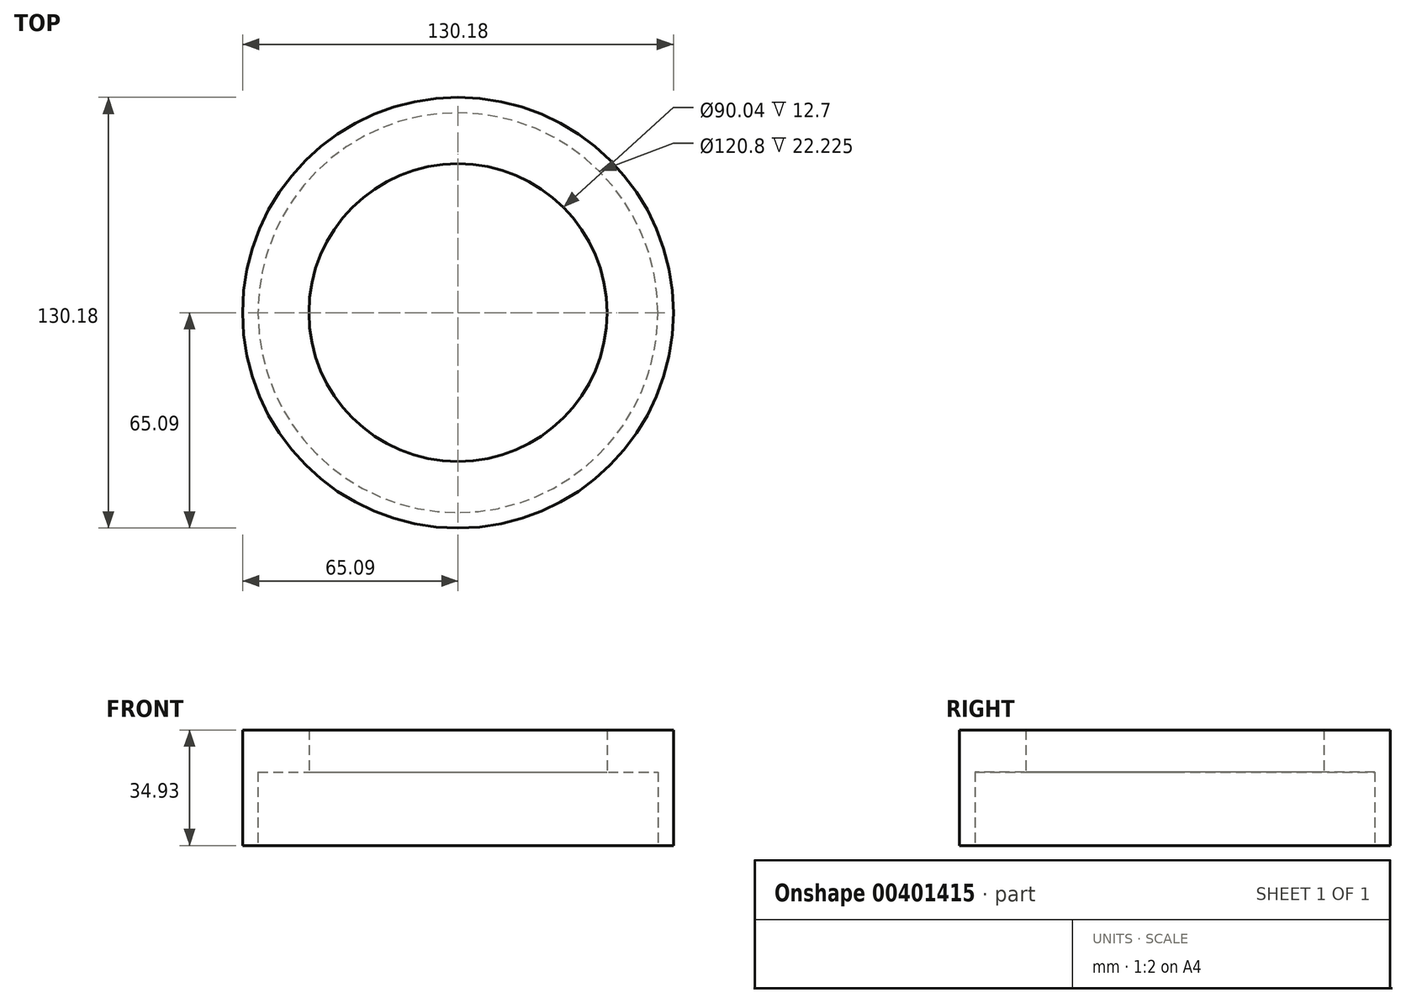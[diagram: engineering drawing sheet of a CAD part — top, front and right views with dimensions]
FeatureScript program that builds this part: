
annotation { "Feature Type Name" : "Feature", "Feature Type Description" : "" }
export const myFeature = defineFeature(function(context is Context, id is Id, definition is map)
    precondition{}
    {
        {
            var Q0;
            Q0=qCreatedBy(makeId("Top.planeOp"),FACE);
            var sketch = newSketch(context, id + "F0", { "sketchPlane" : qUnion([Q0])});
            skCircle(sketch, "E0", {"center": v(0, 0) * mm, "radius": 65.09 * mm});
            skSolve(sketch);
        }
        {
            var Q0;
            Q0=makeQuery(id+"F0.imprint","IMPRINT",FACE,{"disambiguationData":[TD([[makeQuery(id+"F0.imprint","IMPRINT",EDGE,{"derivedFrom":sQuery(id+"F0.wireOp",EDGE,"E0")}),1.0]])]});
            extrude(context, id + "F1", {"entities" : qUnion([Q0]), "oppositeDirection" : true, "depth" : 34.92 * mm});
        }
        {
            var Q0;
            Q0=makeQuery(id+"F1.opExtrude","CAP_FACE",FACE,{"disambiguationData":[OSD([sQuery(id+"F0.wireOp",EDGE,"E0")])],"isStart":false});
            var sketch = newSketch(context, id + "F2", { "sketchPlane" : qUnion([Q0])});
            skCircle(sketch, "E1", {"center": v(0, 0) * mm, "radius": 60.33 * mm});
            skSolve(sketch);
        }
        {
            var Q0;
            Q0=sQuery(id+"F2.wireOp",VERTEX,"E1.center");
            var Q1;
            Q1=makeQuery(id+"F1.opExtrude","SWEPT_BODY",BODY,{"disambiguationData":[OSD([sQuery(id+"F0.wireOp",EDGE,"E0")])]});
            hole(context, id + "F3", {"style" : HoleStyle.C_BORE, "endStyle" : HoleEndStyle.BLIND, "holeDiameter" : 90.04 * mm, "cBoreDiameter" : 120.8 * mm, "cBoreDepth" : 22.22 * mm, "holeDepth" : 34.92 * mm, "isTappedThrough" : true, "tappedDepth" : 12.7 * mm, "tapClearance" : 3, "startFromSketch" : true, "locations" : qUnion([Q0]), "scope" : qUnion([Q1])});
        }
    });
